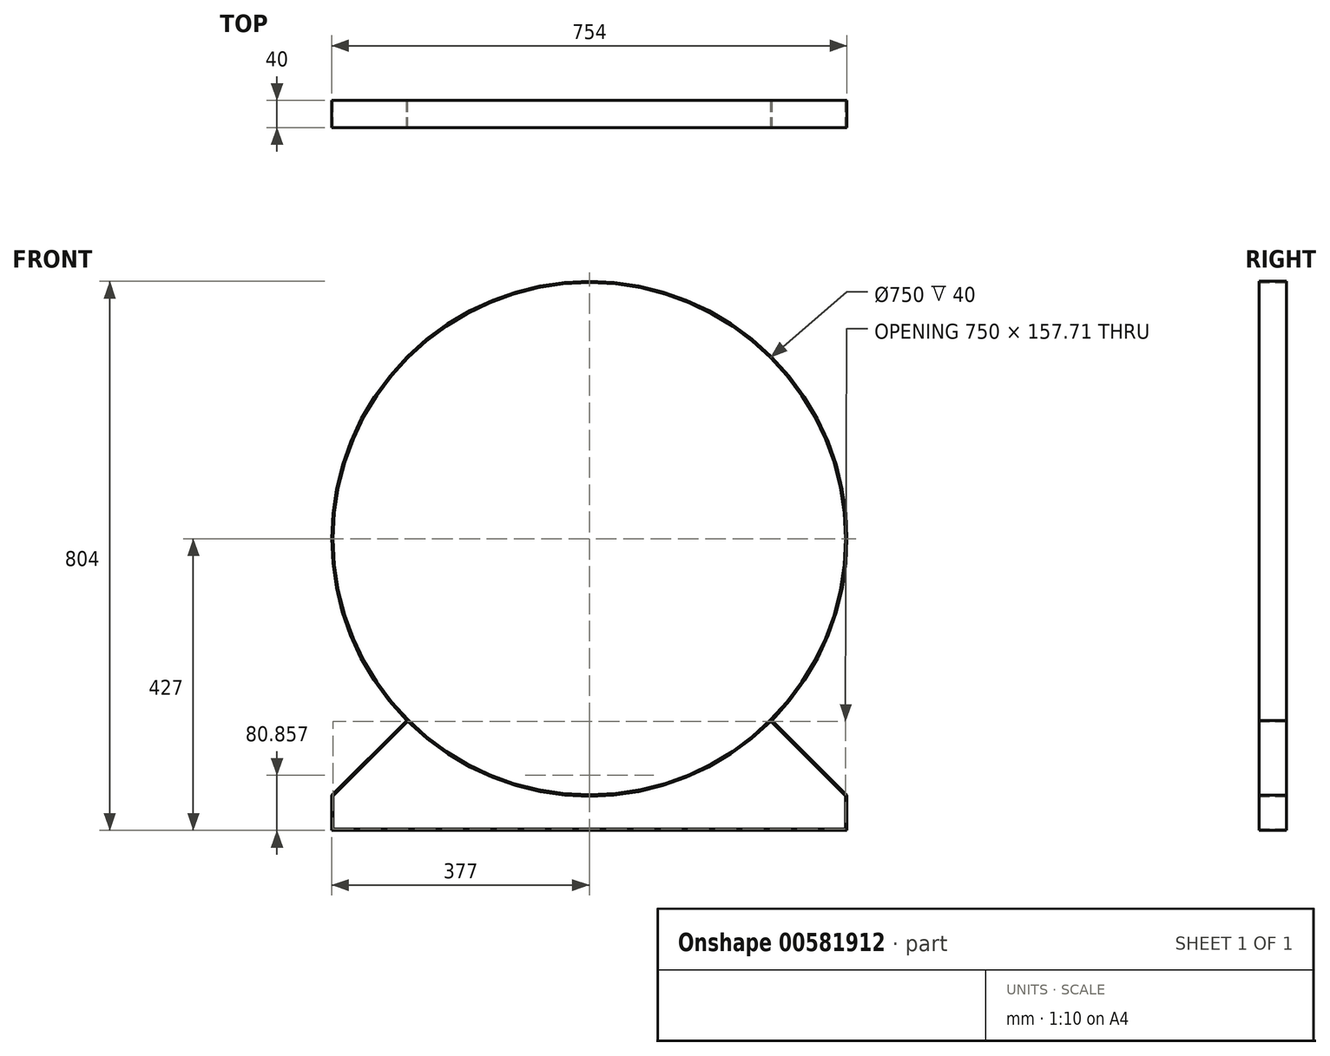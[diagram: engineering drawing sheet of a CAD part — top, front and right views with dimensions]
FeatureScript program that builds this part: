
annotation { "Feature Type Name" : "Feature", "Feature Type Description" : "" }
export const myFeature = defineFeature(function(context is Context, id is Id, definition is map)
    precondition{}
    {
        {
            var Q0;
            Q0=qCreatedBy(makeId("Front.planeOp"),FACE);
            var sketch = newSketch(context, id + "F0", { "sketchPlane" : qUnion([Q0])});
            skLineSegment(sketch, "E0", {"start": v(0, 0) * mm, "end": v(-679.96, 0) * mm, "construction": true});
            skLineSegment(sketch, "E1", {"start": v(0, 0) * mm, "end": v(0, 658.78) * mm, "construction": true});
            skLineSegment(sketch, "E2", {"start": v(0, 0) * mm, "end": v(-291.77, -291.77) * mm, "construction": true});
            skLineSegment(sketch, "E3", {"start": v(0, 0) * mm, "end": v(291.77, -291.77) * mm, "construction": true});
            skCircle(sketch, "E4", {"center": v(0, 0) * mm, "radius": 375 * mm});
            skCircle(sketch, "E5", {"center": v(0, 0) * mm, "radius": 377 * mm});
            skLineSegment(sketch, "E6", {"start": v(-377, -427) * mm, "end": v(0, -427) * mm});
            skLineSegment(sketch, "E7", {"start": v(-375, -425) * mm, "end": v(0, -425) * mm});
            skLineSegment(sketch, "E8", {"start": v(0, 0) * mm, "end": v(0, -311.11) * mm, "construction": true});
            skLineSegment(sketch, "E9", {"start": v(-375, -425) * mm, "end": v(-375, -376.41) * mm});
            skLineSegment(sketch, "E10", {"start": v(-377, -427) * mm, "end": v(-377, -375.59) * mm});
            skLineSegment(sketch, "E11", {"start": v(-267.29, -265.87) * mm, "end": v(-377, -375.59) * mm});
            skLineSegment(sketch, "E12", {"start": v(-265.87, -267.29) * mm, "end": v(-375, -376.41) * mm});
            skLineSegment(sketch, "E13.MirrorCS", {"start": v(265.87, -267.29) * mm, "end": v(375, -376.41) * mm});
            skLineSegment(sketch, "E14.MirrorCS", {"start": v(377, -427) * mm, "end": v(0, -427) * mm});
            skLineSegment(sketch, "E15.MirrorCS", {"start": v(375, -425) * mm, "end": v(0, -425) * mm});
            skLineSegment(sketch, "E16.MirrorCS", {"start": v(267.29, -265.87) * mm, "end": v(377, -375.59) * mm});
            skLineSegment(sketch, "E17.MirrorCS", {"start": v(375, -425) * mm, "end": v(375, -376.41) * mm});
            skLineSegment(sketch, "E18.MirrorCS", {"start": v(377, -427) * mm, "end": v(377, -375.59) * mm});
            skSolve(sketch);
        }
        {
            var Q0;
            Q0=qSketchRegion(id+"F0",true);
            extrude(context, id + "F1", {"entities" : qUnion([Q0]), "offsetDistance" : 25 * mm, "depth" : 40 * mm});
        }
    });
